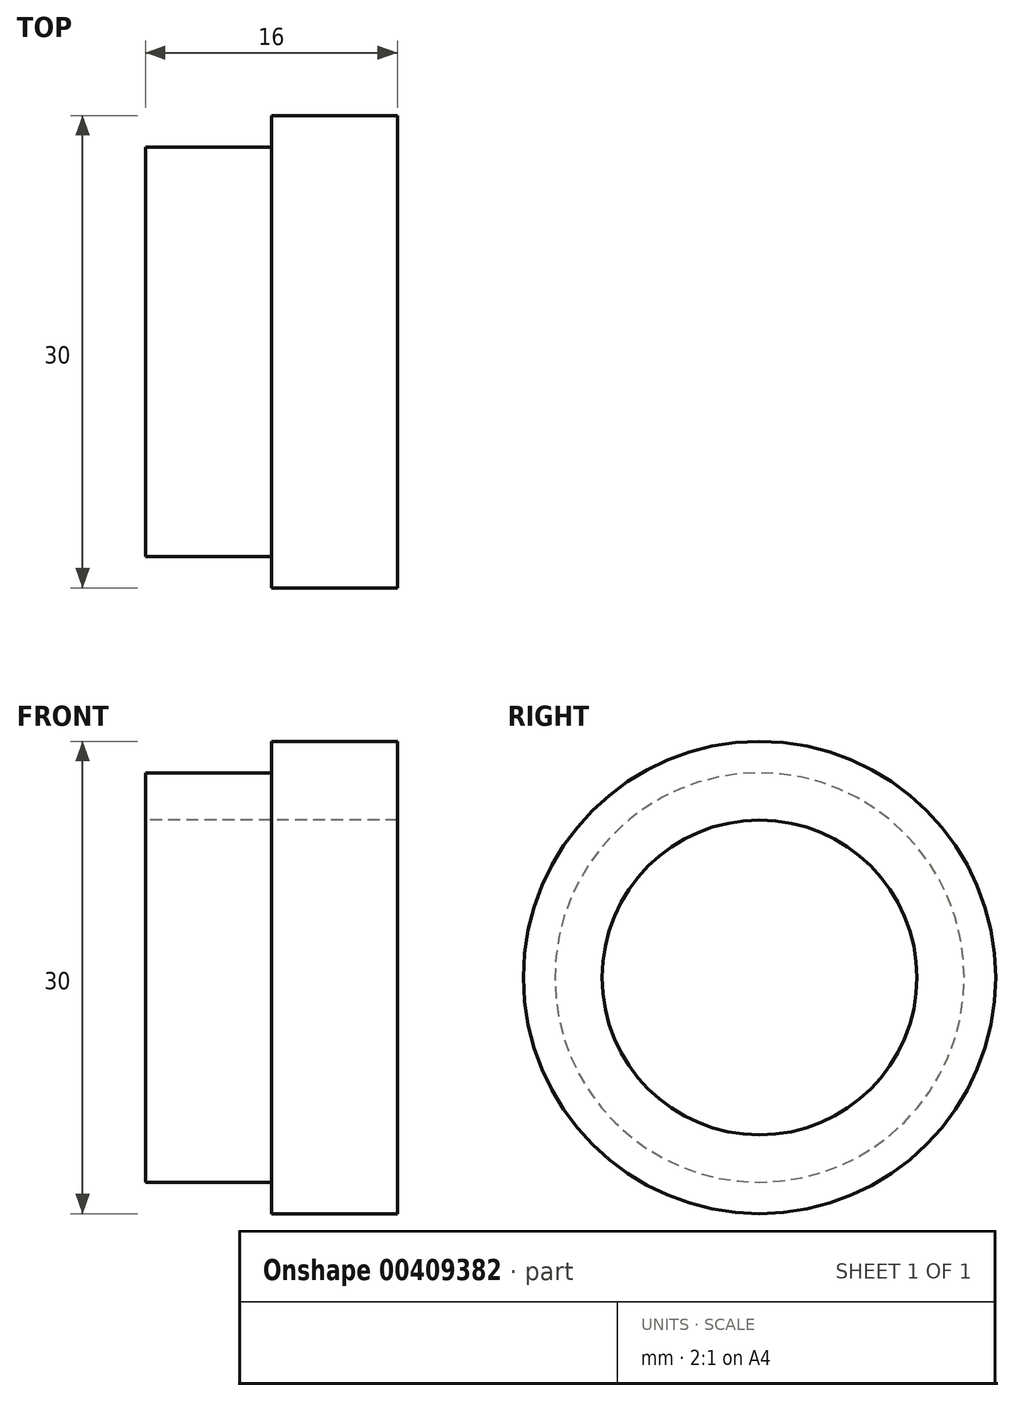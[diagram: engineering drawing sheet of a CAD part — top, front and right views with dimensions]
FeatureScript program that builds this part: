
annotation { "Feature Type Name" : "Feature", "Feature Type Description" : "" }
export const myFeature = defineFeature(function(context is Context, id is Id, definition is map)
    precondition{}
    {
        {
            var Q0;
            Q0=qCreatedBy(makeId("Front.planeOp"),FACE);
            var sketch = newSketch(context, id + "F0", { "sketchPlane" : qUnion([Q0])});
            skLineSegment(sketch, "E0", {"start": v(0, 10) * mm, "end": v(16, 10) * mm});
            skLineSegment(sketch, "E1", {"start": v(16, 10) * mm, "end": v(16, 15) * mm});
            skLineSegment(sketch, "E2", {"start": v(16, 15) * mm, "end": v(8, 15) * mm});
            skLineSegment(sketch, "E3", {"start": v(8, 15) * mm, "end": v(8, 13) * mm});
            skLineSegment(sketch, "E4", {"start": v(8, 13) * mm, "end": v(0, 13) * mm});
            skLineSegment(sketch, "E5", {"start": v(0, 13) * mm, "end": v(0, 10) * mm});
            skLineSegment(sketch, "E6", {"start": v(0, 0) * mm, "end": v(31.72, 0) * mm, "construction": true});
            skSolve(sketch);
        }
        {
            var Q0;
            Q0=makeQuery(id+"F0.imprint","IMPRINT",FACE,{"disambiguationData":[TD([[makeQuery(id+"F0.imprint","IMPRINT",EDGE,{"derivedFrom":sQuery(id+"F0.wireOp",EDGE,"E0")}),1.0]])]});
            var Q1;
            Q1=sQuery(id+"F0.wireOp",EDGE,"E6");
            revolve(context, id + "F1", {"entities" : qUnion([Q0]), "axis" : qUnion([Q1]), "revolveType" : RevolveType.FULL});
        }
    });
